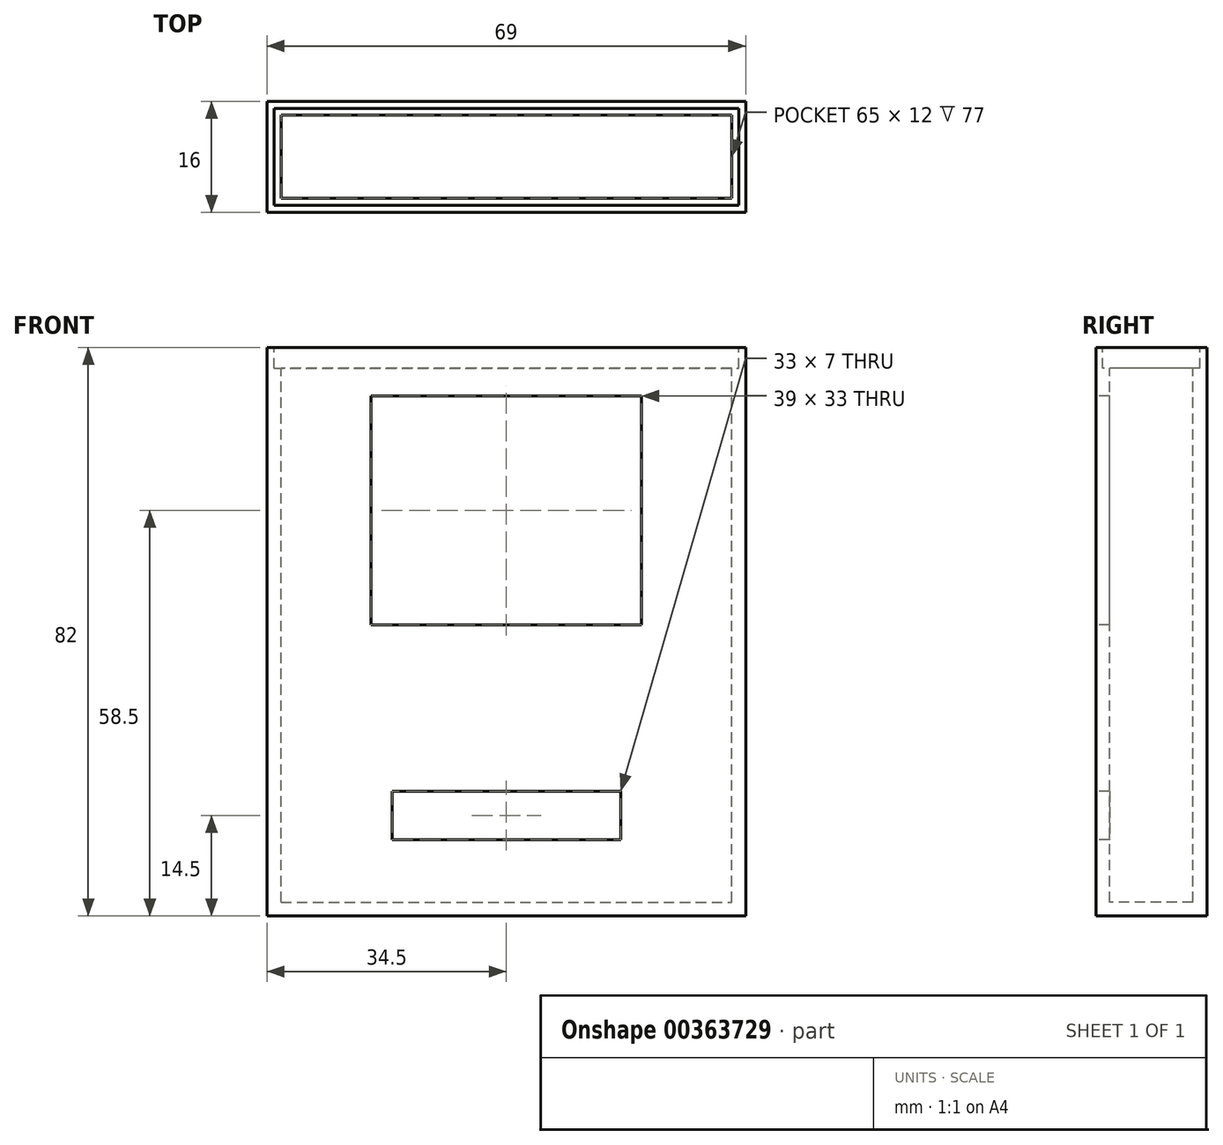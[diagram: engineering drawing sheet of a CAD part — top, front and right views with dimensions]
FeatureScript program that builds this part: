
annotation { "Feature Type Name" : "Feature", "Feature Type Description" : "" }
export const myFeature = defineFeature(function(context is Context, id is Id, definition is map)
    precondition{}
    {
        {
            var Q0;
            Q0=qCreatedBy(makeId("Front.planeOp"),FACE);
            var sketch = newSketch(context, id + "F0", { "sketchPlane" : qUnion([Q0])});
            skLineSegment(sketch, "E0.bottom", {"start": v(0, 0) * mm, "end": v(65, 0) * mm});
            skLineSegment(sketch, "E0.top", {"start": v(0, 80) * mm, "end": v(65, 80) * mm});
            skLineSegment(sketch, "E0.left", {"start": v(0, 0) * mm, "end": v(0, 80) * mm});
            skLineSegment(sketch, "E0.right", {"start": v(65, 0) * mm, "end": v(65, 80) * mm});
            skSolve(sketch);
        }
        {
            var Q0;
            Q0=makeQuery(id+"F0.imprint","IMPRINT",FACE,{"disambiguationData":[TD([[makeQuery(id+"F0.imprint","IMPRINT",EDGE,{"derivedFrom":sQuery(id+"F0.wireOp",EDGE,"E0.bottom")}),1.0]])]});
            extrude(context, id + "F1", {"entities" : qUnion([Q0]), "oppositeDirection" : true, "depth" : 12 * mm});
        }
        {
            var Q0;
            Q0=makeQuery(id+"F1.opExtrude","SWEPT_FACE",FACE,{"disambiguationData":[OSD([sQuery(id+"F0.wireOp",EDGE,"E0.top")])]});
            shell(context, id + "F2", {"entities" : qUnion([Q0]), "thickness" : 2 * mm, "oppositeDirection" : true});
        }
        {
            var Q0;
            Q0=makeQuery(id+"F1.opExtrude","SWEPT_FACE",FACE,{"disambiguationData":[OSD([sQuery(id+"F0.wireOp",EDGE,"E0.top")])]});
            var sketch = newSketch(context, id + "F3", { "sketchPlane" : qUnion([Q0])});
            skLineSegment(sketch, "E1.bottom", {"start": v(-1, 13) * mm, "end": v(66, 13) * mm});
            skLineSegment(sketch, "E1.top", {"start": v(-1, -1) * mm, "end": v(66, -1) * mm});
            skLineSegment(sketch, "E1.left", {"start": v(-1, 13) * mm, "end": v(-1, -1) * mm});
            skLineSegment(sketch, "E1.right", {"start": v(66, 13) * mm, "end": v(66, -1) * mm});
            skSolve(sketch);
        }
        {
            var Q0;
            Q0 = qSketchRegion(id + "F3", true);
            extrude(context, id + "F4", {"entities" : qUnion([Q0]), "operationType" : NewBodyOperationType.REMOVE, "oppositeDirection" : true, "depth" : 3 * mm});
        }
        {
            var Q0;
            Q0=makeQuery(id+"F1.opExtrude","CAP_FACE",FACE,{"disambiguationData":[OSD([sQuery(id+"F0.wireOp",EDGE,"E0.bottom"),sQuery(id+"F0.wireOp",EDGE,"E0.top"),sQuery(id+"F0.wireOp",EDGE,"E0.left"),sQuery(id+"F0.wireOp",EDGE,"E0.right")])],"isStart":true});
            var sketch = newSketch(context, id + "F5", { "sketchPlane" : qUnion([Q0])});
            skLineSegment(sketch, "E2.bottom", {"start": v(16, 9) * mm, "end": v(49, 9) * mm});
            skLineSegment(sketch, "E2.top", {"start": v(16, 16) * mm, "end": v(49, 16) * mm});
            skLineSegment(sketch, "E2.left", {"start": v(16, 9) * mm, "end": v(16, 16) * mm});
            skLineSegment(sketch, "E2.right", {"start": v(49, 9) * mm, "end": v(49, 16) * mm});
            skLineSegment(sketch, "E3.bottom", {"start": v(13, 73) * mm, "end": v(52, 73) * mm});
            skLineSegment(sketch, "E3.top", {"start": v(13, 40) * mm, "end": v(52, 40) * mm});
            skLineSegment(sketch, "E3.left", {"start": v(13, 73) * mm, "end": v(13, 40) * mm});
            skLineSegment(sketch, "E3.right", {"start": v(52, 73) * mm, "end": v(52, 40) * mm});
            skSolve(sketch);
        }
        {
            var Q0;
            Q0 = qSketchRegion(id + "F5", true);
            extrude(context, id + "F6", {"entities" : qUnion([Q0]), "operationType" : NewBodyOperationType.REMOVE, "endBound" : BoundingType.UP_TO_NEXT, "oppositeDirection" : true, "depth" : 25 * mm});
        }
    });
